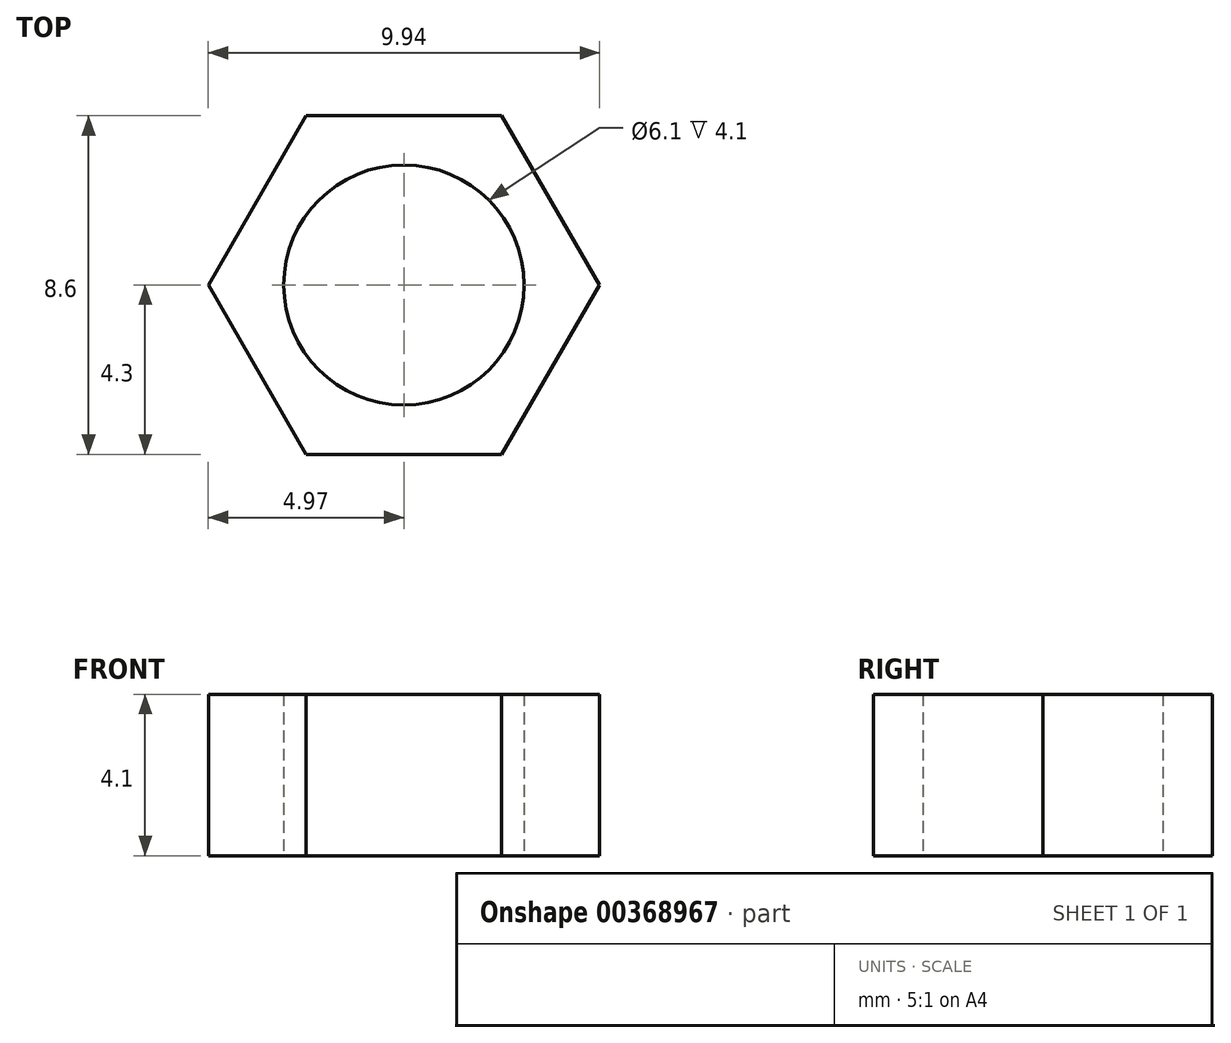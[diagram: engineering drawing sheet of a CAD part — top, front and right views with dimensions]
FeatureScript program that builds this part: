
annotation { "Feature Type Name" : "Feature", "Feature Type Description" : "" }
export const myFeature = defineFeature(function(context is Context, id is Id, definition is map)
    precondition{}
    {
        {
            var Q0;
            Q0=qCreatedBy(makeId("Top.planeOp"),FACE);
            var sketch = newSketch(context, id + "F0", { "sketchPlane" : qUnion([Q0])});
            skCircle(sketch, "E0.cCircle", {"center": v(0, 0) * mm, "radius": 4.3 * mm, "construction": true});
            skLineSegment(sketch, "E0.0", {"start": v(2.48, -4.3) * mm, "end": v(-2.48, -4.3) * mm});
            skLineSegment(sketch, "E0.1", {"start": v(-2.48, -4.3) * mm, "end": v(-4.97, 0) * mm});
            skLineSegment(sketch, "E0.2", {"start": v(-4.97, 0) * mm, "end": v(-2.48, 4.3) * mm});
            skLineSegment(sketch, "E0.3", {"start": v(-2.48, 4.3) * mm, "end": v(2.48, 4.3) * mm});
            skLineSegment(sketch, "E0.4", {"start": v(2.48, 4.3) * mm, "end": v(4.97, 0) * mm});
            skLineSegment(sketch, "E0.5", {"start": v(4.97, 0) * mm, "end": v(2.48, -4.3) * mm});
            skPoint(sketch, "E0.0.midPoint", {"position": v(0, -4.3) * mm});
            skCircle(sketch, "E1", {"center": v(0, 0) * mm, "radius": 3.05 * mm});
            skSolve(sketch);
        }
        {
            var Q0;
            Q0=makeQuery(id+"F0.imprint","IMPRINT",FACE,{"disambiguationData":[TD([[makeQuery(id+"F0.imprint","IMPRINT",EDGE,{"derivedFrom":sQuery(id+"F0.wireOp",EDGE,"E0.0")}),-1.0]])]});
            extrude(context, id + "F1", {"entities" : qUnion([Q0]), "depth" : 4.1 * mm});
        }
    });
